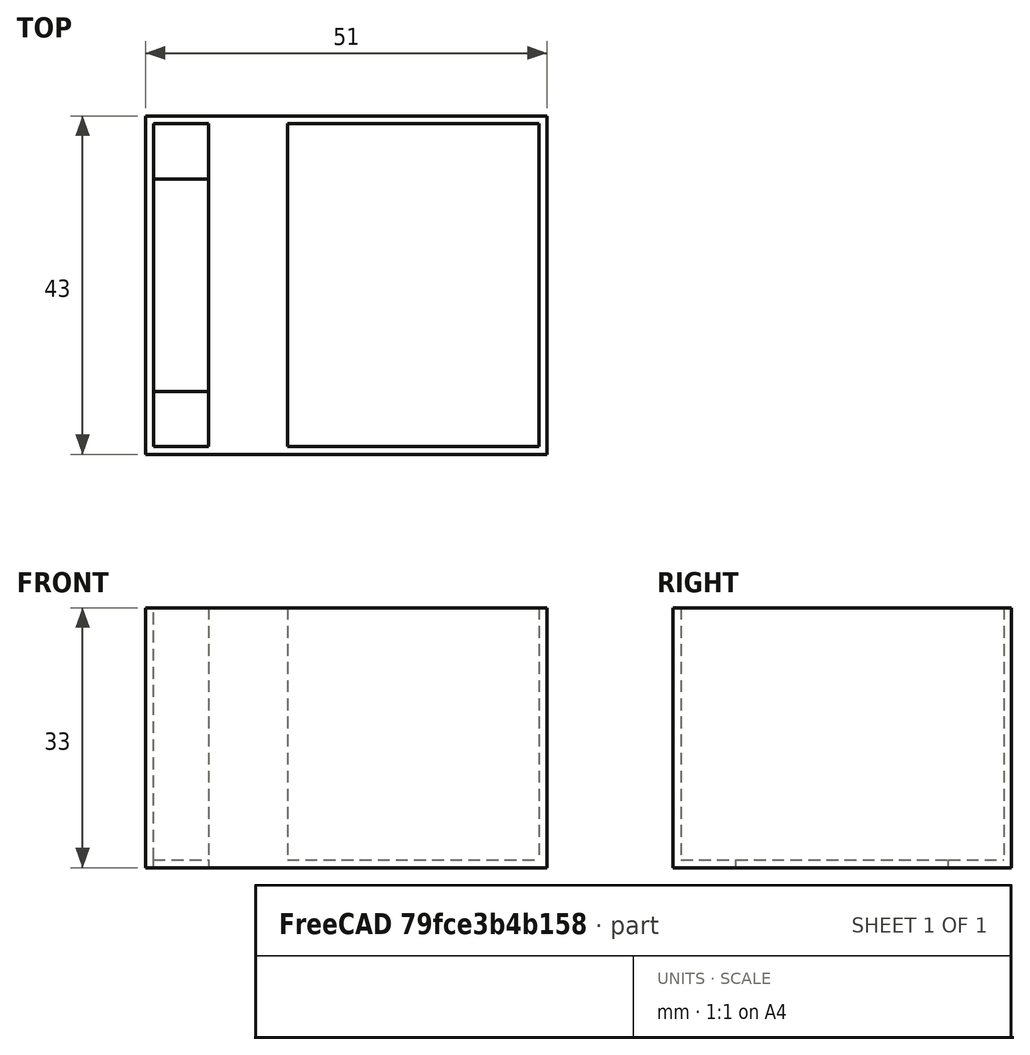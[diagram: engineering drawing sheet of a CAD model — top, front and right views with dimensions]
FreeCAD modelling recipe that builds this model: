
FCSTD DOCUMENT  (FreeCAD 0.18R4 (GitTag))
Label: fireland
License: All rights reserved
LicenseURL: http://en.wikipedia.org/wiki/All_rights_reserved
objects: Part::Box×8, Part::MultiFuse×3, Part::Cut×2
note: 13 computed .brp shape members not serialized (recipe doc carries the construction recipe); baked Part::Feature solids carry a one-line shape summary decoded from their .brp

FEATURE [Part::Box] Box  label="Cube"
  AttacherType = Attacher::AttachEngine3D
  Height = 33
  Length = 202
  Width = 43
FEATURE [Part::Box] Box001  label="Cube001"
  AttacherType = Attacher::AttachEngine3D
  Height = 33
  Length = 200
  Placement = pos=(1,1,0) rot=(0,0,1;0rad)
  Width = 41
FEATURE [Part::Cut] Cut
  Base = -> Box
  Tool = -> Box001
FEATURE [Part::Box] Box002  label="Cube002"
  AttacherType = Attacher::AttachEngine3D
  Height = 1
  Length = 202
  Width = 8
FEATURE [Part::Box] Box003  label="Cube003"
  AttacherType = Attacher::AttachEngine3D
  Height = 1
  Length = 202
  Placement = pos=(0,35,0) rot=(0,0,1;0rad)
  Width = 8
FEATURE [Part::MultiFuse] Fusion
  Shapes = -> [Cut,Box002,Box003]
FEATURE [Part::Box] Box004  label="Cube004"
  AttacherType = Attacher::AttachEngine3D
  Height = 33
  Length = 10
  Placement = pos=(8,0,0) rot=(0,0,1;0rad)
  Width = 43
FEATURE [Part::Box] Box005  label="Cube005"
  AttacherType = Attacher::AttachEngine3D
  Height = 33
  Length = 10
  Placement = pos=(50,0,0) rot=(0,0,1;0rad)
  Width = 43
FEATURE [Part::Box] Box006  label="Cube006"
  AttacherType = Attacher::AttachEngine3D
  Height = 33
  Length = 151
  Placement = pos=(51,0,0) rot=(0,0,1;0rad)
  Width = 43
FEATURE [Part::MultiFuse] Fusion001
  Shapes = -> [Fusion,Box004,Box005]
FEATURE [Part::Cut] Cut001
  Base = -> Fusion001
  Tool = -> Box006
FEATURE [Part::Box] Box007  label="Cube007"
  AttacherType = Attacher::AttachEngine3D
  Height = 1
  Length = 32
  Placement = pos=(18,0,0) rot=(0,0,1;0rad)
  Width = 43
FEATURE [Part::MultiFuse] Fusion002
  Shapes = -> [Box007,Cut001]
